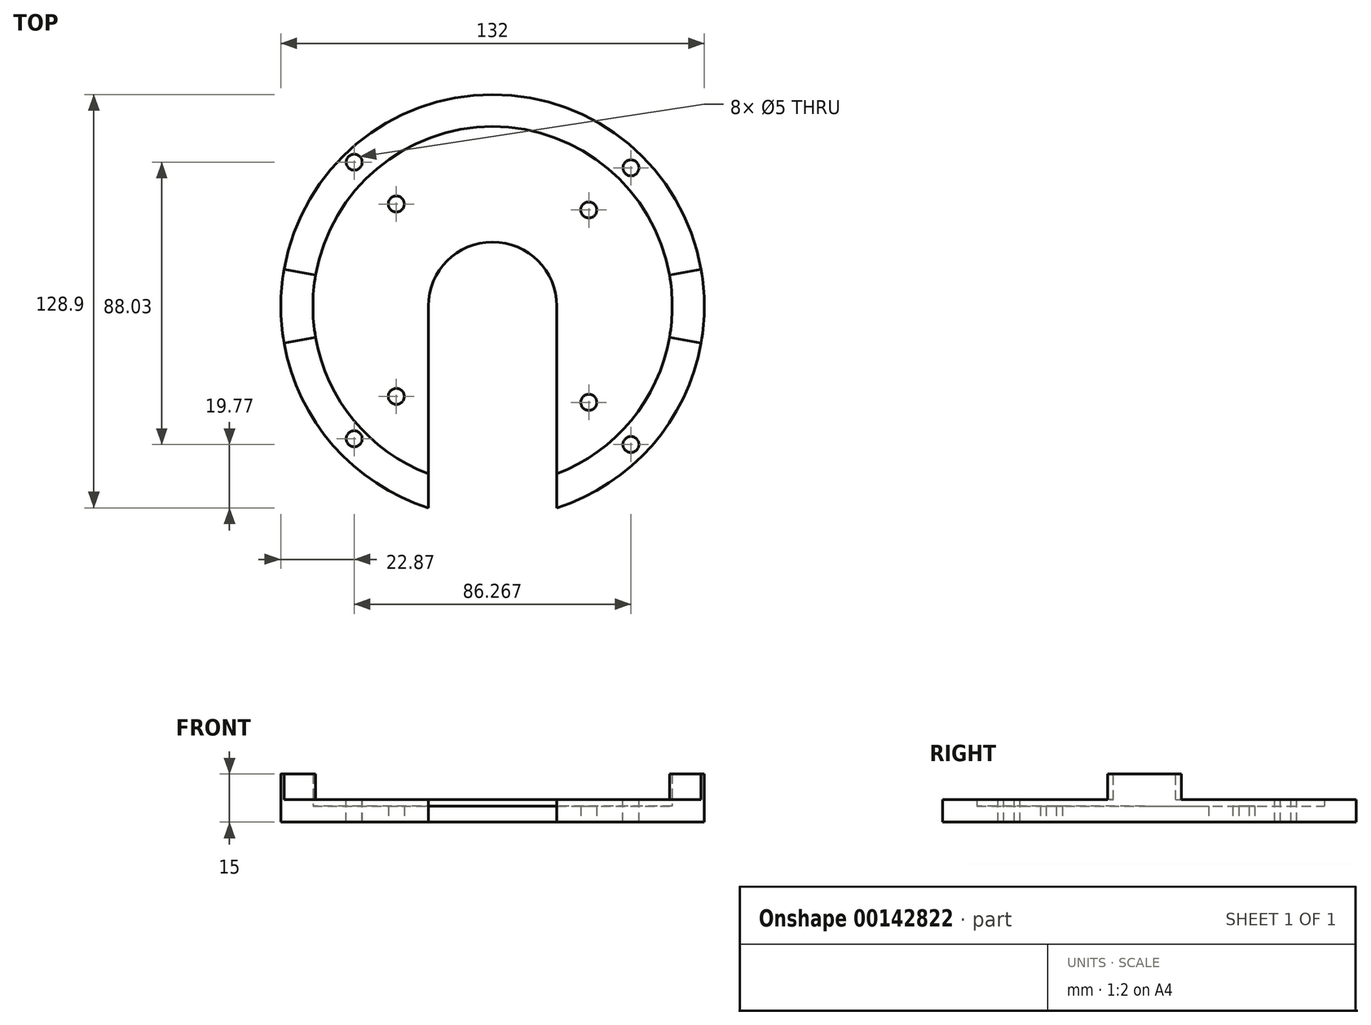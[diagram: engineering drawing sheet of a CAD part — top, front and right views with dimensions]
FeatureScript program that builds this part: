
annotation { "Feature Type Name" : "Feature", "Feature Type Description" : "" }
export const myFeature = defineFeature(function(context is Context, id is Id, definition is map)
    precondition{}
    {
        {
            var Q0;
            Q0=qCreatedBy(makeId("Top.planeOp"),FACE);
            var sketch = newSketch(context, id + "F0", { "sketchPlane" : qUnion([Q0])});
            skArc(sketch, "E0", {"start": v(20, -62.9) * mm, "mid": v(0, 66) * mm, "end": v(-20, -62.9) * mm});
            skArc(sketch, "E1", {"start": v(20, -52.3) * mm, "mid": v(0, 56) * mm, "end": v(-20, -52.3) * mm});
            skArc(sketch, "E2", {"start": v(20, 0) * mm, "mid": v(0, 20) * mm, "end": v(-20, 0) * mm});
            skLineSegment(sketch, "E3", {"start": v(-20, 0) * mm, "end": v(-20, -62.9) * mm});
            skLineSegment(sketch, "E4", {"start": v(20, 0) * mm, "end": v(20, -62.9) * mm});
            skSolve(sketch);
        }
        {
            var Q0;
            {var subQ0=sQuery(id+"F0.wireOp",EDGE,"E0");Q0=makeQuery(id+"F0.imprint","IMPRINT",FACE,{"disambiguationData":[TD([[makeQuery(id+"F0.imprint","IMPRINT",EDGE,{"derivedFrom":subQ0}),1.0]])]});}
            extrude(context, id + "F1", {"entities" : qUnion([Q0]), "depth" : 15 * mm, "offsetDistance" : 25 * mm});
        }
        {
            var Q0;
            Q0=qCreatedBy(makeId("Top.planeOp"),FACE);
            var sketch = newSketch(context, id + "F2", { "sketchPlane" : qUnion([Q0])});
            skArc(sketch, "E5", {"start": v(20, -52.3) * mm, "mid": v(0, 56) * mm, "end": v(-20, -52.3) * mm});
            skArc(sketch, "E6", {"start": v(20, 0) * mm, "mid": v(0, 20) * mm, "end": v(-20, 0) * mm});
            skLineSegment(sketch, "E7", {"start": v(-20, 0) * mm, "end": v(-20, -52.3) * mm});
            skLineSegment(sketch, "E8", {"start": v(20, 0) * mm, "end": v(20, -52.3) * mm});
            skSolve(sketch);
        }
        {
            var Q0;
            Q0 = qSketchRegion(id + "F2", true);
            extrude(context, id + "F3", {"entities" : qUnion([Q0]), "operationType" : NewBodyOperationType.ADD, "depth" : 5 * mm, "offsetDistance" : 25 * mm});
        }
        {
            var Q0;
            Q0=makeQuery(id+"F1.opExtrude","CAP_FACE",FACE,{"disambiguationData":[OSD([sQuery(id+"F0.wireOp",EDGE,"E0"),sQuery(id+"F0.wireOp",EDGE,"E1"),sQuery(id+"F0.wireOp",EDGE,"E3"),sQuery(id+"F0.wireOp",EDGE,"E4")])],"isStart":false});
            var sketch = newSketch(context, id + "F4", { "sketchPlane" : qUnion([Q0])});
            skLineSegment(sketch, "E9", {"start": v(-55.15, 9.72) * mm, "end": v(-65, 11.46) * mm});
            skLineSegment(sketch, "E10", {"start": v(-55.15, -9.72) * mm, "end": v(-65, -11.46) * mm});
            skLineSegment(sketch, "E11", {"start": v(55.15, 9.72) * mm, "end": v(65, 11.46) * mm});
            skLineSegment(sketch, "E12", {"start": v(55.15, -9.72) * mm, "end": v(65, -11.46) * mm});
            skArc(sketch, "E13", {"start": v(-65, -11.46) * mm, "mid": v(66, 0) * mm, "end": v(-65, 11.46) * mm});
            skArc(sketch, "E14", {"start": v(55.15, 9.72) * mm, "mid": v(0, 56) * mm, "end": v(-55.15, 9.72) * mm});
            skLineSegment(sketch, "E15", {"start": v(-20, -52.3) * mm, "end": v(-20, -62.9) * mm});
            skLineSegment(sketch, "E16", {"start": v(20, -52.3) * mm, "end": v(20, -62.9) * mm});
            skPoint(sketch, "E17.orphan", {"position": v(-20, -34.48) * mm});
            skPoint(sketch, "E18.orphan", {"position": v(20, -34.48) * mm});
            skArc(sketch, "E19.trimOffspring", {"start": v(-55.15, -9.72) * mm, "mid": v(0, -56) * mm, "end": v(55.15, -9.72) * mm});
            skSolve(sketch);
        }
        {
            var Q0;
            Q0 = qSketchRegion(id + "F4", true);
            extrude(context, id + "F5", {"entities" : qUnion([Q0]), "operationType" : NewBodyOperationType.REMOVE, "depth" : -8 * mm, "offsetDistance" : 25 * mm});
        }
        {
            var Q0;
            Q0=makeQuery(id+"F3.opExtrude","CAP_FACE",FACE,{"disambiguationData":[OSD([sQuery(id+"F2.wireOp",EDGE,"E5"),sQuery(id+"F2.wireOp",EDGE,"E6"),sQuery(id+"F2.wireOp",EDGE,"E7"),sQuery(id+"F2.wireOp",EDGE,"E8")])],"isStart":false});
            var sketch = newSketch(context, id + "F6", { "sketchPlane" : qUnion([Q0])});
            skPoint(sketch, "E20", {"position": v(30, -30) * mm});
            skPoint(sketch, "E21", {"position": v(30, 30) * mm});
            skPoint(sketch, "E22", {"position": v(-30, 31.86) * mm});
            skPoint(sketch, "E23", {"position": v(-30, -28.14) * mm});
            skSolve(sketch);
        }
        {
            var Q0;
            Q0=qCreatedBy(makeId("Top.planeOp"),FACE);
            var sketch = newSketch(context, id + "F7", { "sketchPlane" : qUnion([Q0])});
            skPoint(sketch, "E24", {"position": v(43.14, 43.13) * mm});
            skPoint(sketch, "E25", {"position": v(-43.12, 44.9) * mm});
            skPoint(sketch, "E26", {"position": v(-43.13, -41.36) * mm});
            skPoint(sketch, "E27", {"position": v(43.13, -43.13) * mm});
            skSolve(sketch);
        }
        {
            var Q0;
            Q0=sQuery(id+"F7.wireOp",VERTEX,"E27");
            var Q1;
            Q1=sQuery(id+"F7.wireOp",VERTEX,"E24");
            var Q2;
            Q2=sQuery(id+"F7.wireOp",VERTEX,"E26");
            var Q3;
            Q3=sQuery(id+"F7.wireOp",VERTEX,"E25");
            var Q4;
            Q4=makeQuery(id+"F1.opExtrude","SWEPT_BODY",BODY,{"disambiguationData":[OSD([sQuery(id+"F0.wireOp",EDGE,"E0"),sQuery(id+"F0.wireOp",EDGE,"E1"),sQuery(id+"F0.wireOp",EDGE,"E3"),sQuery(id+"F0.wireOp",EDGE,"E4")])]});
            hole(context, id + "F8", {"style" : HoleStyle.SIMPLE, "endStyle" : HoleEndStyle.THROUGH, "oppositeDirection" : true, "holeDiameter" : 5 * mm, "majorDiameter" : 5 * mm, "isTappedThrough" : true, "tappedDepth" : 12 * mm, "tapClearance" : 3, "locations" : qUnion([Q0, Q1, Q2, Q3]), "scope" : qUnion([Q4]), "startStyle" : HoleStartStyle.SKETCH});
        }
        {
            var Q0;
            Q0=sQuery(id+"F6.wireOp",VERTEX,"E20");
            var Q1;
            Q1=sQuery(id+"F6.wireOp",VERTEX,"E21");
            var Q2;
            Q2=sQuery(id+"F6.wireOp",VERTEX,"E22");
            var Q3;
            Q3=sQuery(id+"F6.wireOp",VERTEX,"E23");
            var Q4;
            Q4=makeQuery(id+"F1.opExtrude","SWEPT_BODY",BODY,{"disambiguationData":[OSD([sQuery(id+"F0.wireOp",EDGE,"E0"),sQuery(id+"F0.wireOp",EDGE,"E1"),sQuery(id+"F0.wireOp",EDGE,"E3"),sQuery(id+"F0.wireOp",EDGE,"E4")])]});
            hole(context, id + "F9", {"style" : HoleStyle.SIMPLE, "endStyle" : HoleEndStyle.THROUGH, "holeDiameter" : 5 * mm, "majorDiameter" : 5 * mm, "isTappedThrough" : true, "tappedDepth" : 12 * mm, "tapClearance" : 3, "locations" : qUnion([Q0, Q1, Q2, Q3]), "scope" : qUnion([Q4]), "startStyle" : HoleStartStyle.SKETCH});
        }
    });
